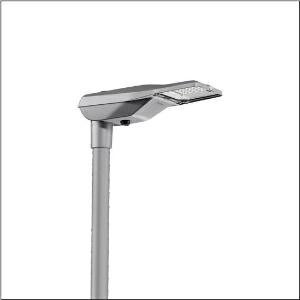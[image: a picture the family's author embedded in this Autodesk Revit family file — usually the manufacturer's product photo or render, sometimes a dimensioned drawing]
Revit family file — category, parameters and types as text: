
# Revit family: streetlight_sl_21_iq_micro___st1_0ab_5xe1m31u08cb_f63b
name_source: partatom
category: Lighting Fixtures
units: mm (PartAtom-declared; Revit-internal decimal feet)

## family parameters
Cut with Voids When Loaded = No
Host = Face
Light Source = No
Part Type = Normal
Room Calculation Point = No
Round Connector Dimension = Use Diameter
Shared = No

## types (1)
- --- (1 x LED, 2530 lm, 19.1 W, 3000K)
    Apparent Load = 19 VA
    CIE Flux Codes = 38 73 97 100 100
    Color Rendering = 70
    Color Temperature = 3000K
    Default Elevation = 1800 mm
    Description = Streetlight SL 21 iQ micro, mast luminaire, primary light control with lens, of PMMA, primary optical cover: cover, of toughened safety glass, transparent, light distribution: ST1.0aB, light emission: direct distribution, primary light characteristic: asymmetric, installation type: post-top, side-entry, LED, High Power LED, rated luminous flux: 2.530lm, luminous efficacy: 133lm/W, light colour: 730, colour temperature: 3000K, control: presetting dimming logarithmic, Street-Remote, Auto-Match, Temp-Guard, Lumen-Switch, Night-Set, Smart-Wire, Light-Fading, Desk-Remote (wireless, voltage-free reading and setting of iQ features in the workshop via application-optimized NFC function/RFID function), optimised constant luminous flux control (CLO 2.0), mains connection: 220..240V, AC, 50/60Hz, start of lifetime: 19W, end of service life: 20W, reduction: 9W, luminaire housing, of diecast aluminium, powder-coated, Siteco® metallic grey (DB 702S), corrosivity category C5 mid according to DIN EN ISO 12944, please order mast flange separately, inclination adjustable: 0°, 5°, 10°, 15°, sealing non-destructively replaceable, multi-level sealing system, length: 528mm, width: 235mm, height: 110mm, mast flange for spigot size: 42mm (side-entry): 5XC10008XM4, 60/48mm (side-entry/post-top): 5XC10108XM2, 76/60mm (side-entry/post-top): 5XC10108XM1, Smart Interface below, protection rating (complete): IP66, insulation class (complete): insulation class II (safety insulation), certification: CE, ENEC, ENEC+, VDE, impact resistance: IK09, permissible operating ambient temperature for outdoor applications: -40..+50°C, standard-compliant lighting for roads and squares, packaging unit: 1 piece

Light Distribution: ST1.0aB
    Height = 110 mm
    Lamp = 1 x LED
    Lamp Light Flux = 2530 lm
    Lamp Power = 19.1 W
    Lamp count = 1
    Length = 528 mm
    Luminous efficacy = 132 lm/W
    Manufacturer = Siteco
    ModVariant = No
    Model = 5XE1M31U08CB
    Number of Poles = 1
    OnlyDefault = Yes
    Power Factor = 1
    Product Name = Streetlight SL 21 iQ micro | ST1.0aB
    Product group = mast luminaire | pylon top
    ProductGroupID = 6100
    Protection Class = Protection class II
    Protection Degree = IP 66
    RLX_Detail_Level = 1
    RLX_Emergency_Light_Flux = 0 lm
    RLX_Emergency_Type = 0
    RLX_Emergency_Type_DB = No
    RlxData = <blob elided: 99321 chars, md5=fce855a8>
    Socket = socket
    Standby Power = 0 W
    System Light Flux = 2530 lm
    System Power = 19 W
    Type Comments = factory setting: luminous flux: 100 % | dim-lin: 254 | 387 mA
    Type Image = l_1277290.jpg
    URL = http://relux.com
    VarID = @adj_061065
    Voltage = 0 V
    Weight = 0.00 kg
    Width = 235 mm

## geometry (parser evidence)
native form markers: Blend x4, Sweep x9
no freeform markers — native parametric forms only
